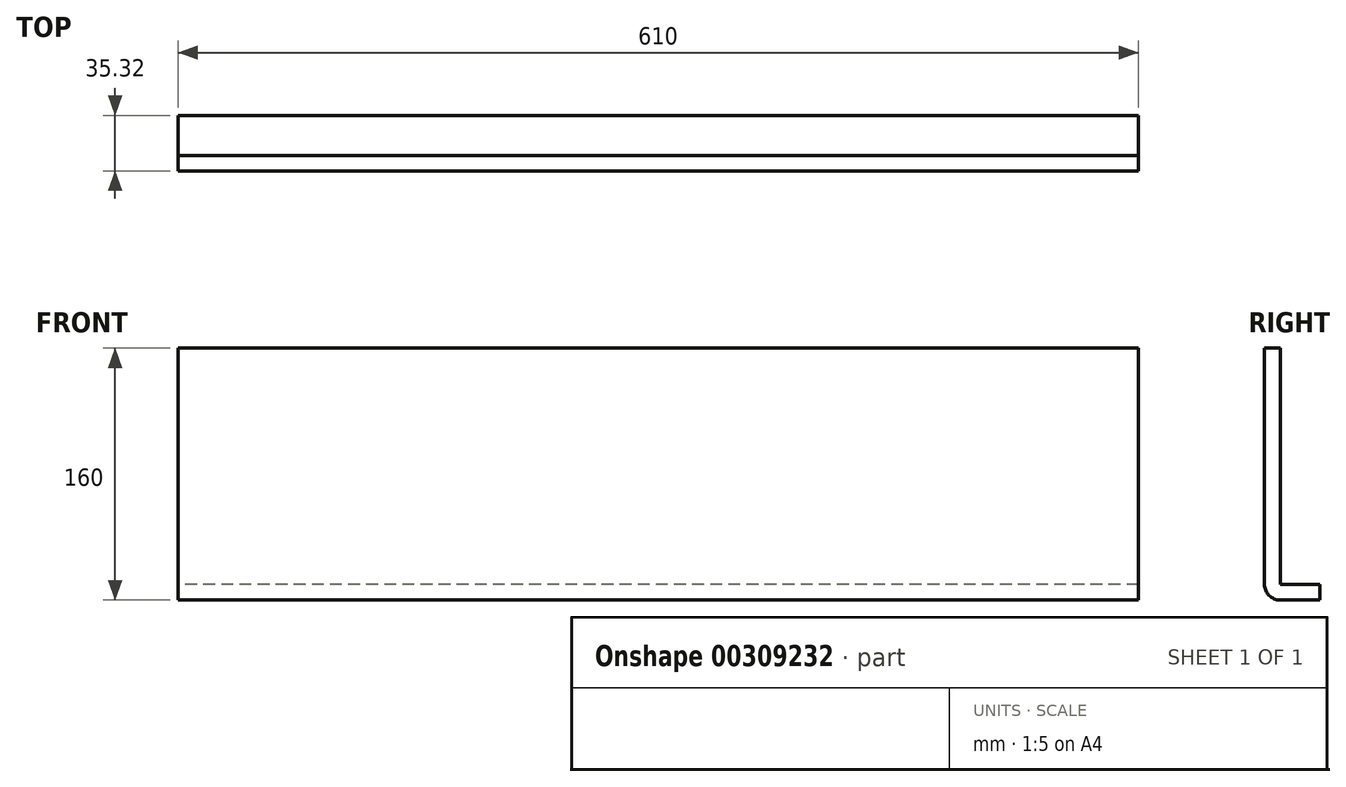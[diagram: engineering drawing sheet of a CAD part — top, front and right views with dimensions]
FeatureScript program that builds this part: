
annotation { "Feature Type Name" : "Feature", "Feature Type Description" : "" }
export const myFeature = defineFeature(function(context is Context, id is Id, definition is map)
    precondition{}
    {
        {
            var Q0;
            Q0=qCreatedBy(makeId("Right.planeOp"),FACE);
            var sketch = newSketch(context, id + "F0", { "sketchPlane" : qUnion([Q0])});
            skLineSegment(sketch, "E0.bottom", {"start": v(0, 0) * mm, "end": v(25.32, 0) * mm});
            skLineSegment(sketch, "E0.left", {"start": v(0, 0) * mm, "end": v(0, 120) * mm});
            skLineSegment(sketch, "E1.0", {"start": v(-10, -10) * mm, "end": v(-10, 120) * mm});
            skLineSegment(sketch, "E1.1", {"start": v(-10, -10) * mm, "end": v(25.32, -10) * mm});
            skLineSegment(sketch, "E2", {"start": v(25.32, 0) * mm, "end": v(25.32, -10) * mm});
            skLineSegment(sketch, "E3", {"start": v(-10, 120) * mm, "end": v(-10, 150) * mm});
            skLineSegment(sketch, "E4", {"start": v(0, 120) * mm, "end": v(0, 150) * mm});
            skPoint(sketch, "E5.orphan", {"position": v(95.32, 0) * mm});
            skLineSegment(sketch, "E6", {"start": v(0, 150) * mm, "end": v(-10, 150) * mm});
            skSolve(sketch);
        }
        {
            var Q0;
            Q0=makeQuery(id+"F0.imprint","IMPRINT",FACE,{"disambiguationData":[TD([[makeQuery(id+"F0.imprint","IMPRINT",EDGE,{"derivedFrom":sQuery(id+"F0.wireOp",EDGE,"E0.bottom")}),-1.0]])]});
            extrude(context, id + "F1", {"entities" : qUnion([Q0]), "depth" : 610 * mm});
        }
        {
            var Q0;
            Q0=makeQuery(id+"F1.opExtrude","SWEPT_EDGE",EDGE,{"disambiguationData":[OSD([sQuery(id+"F0.wireOp",EDGE,"E1.0"),sQuery(id+"F0.wireOp",EDGE,"E1.1")])]});
            fillet(context, id + "F2", {"entities" : qUnion([Q0]), "radius" : 10 * mm, "tangentPropagation" : true, "allowEdgeOverflow" : false});
        }
    });
